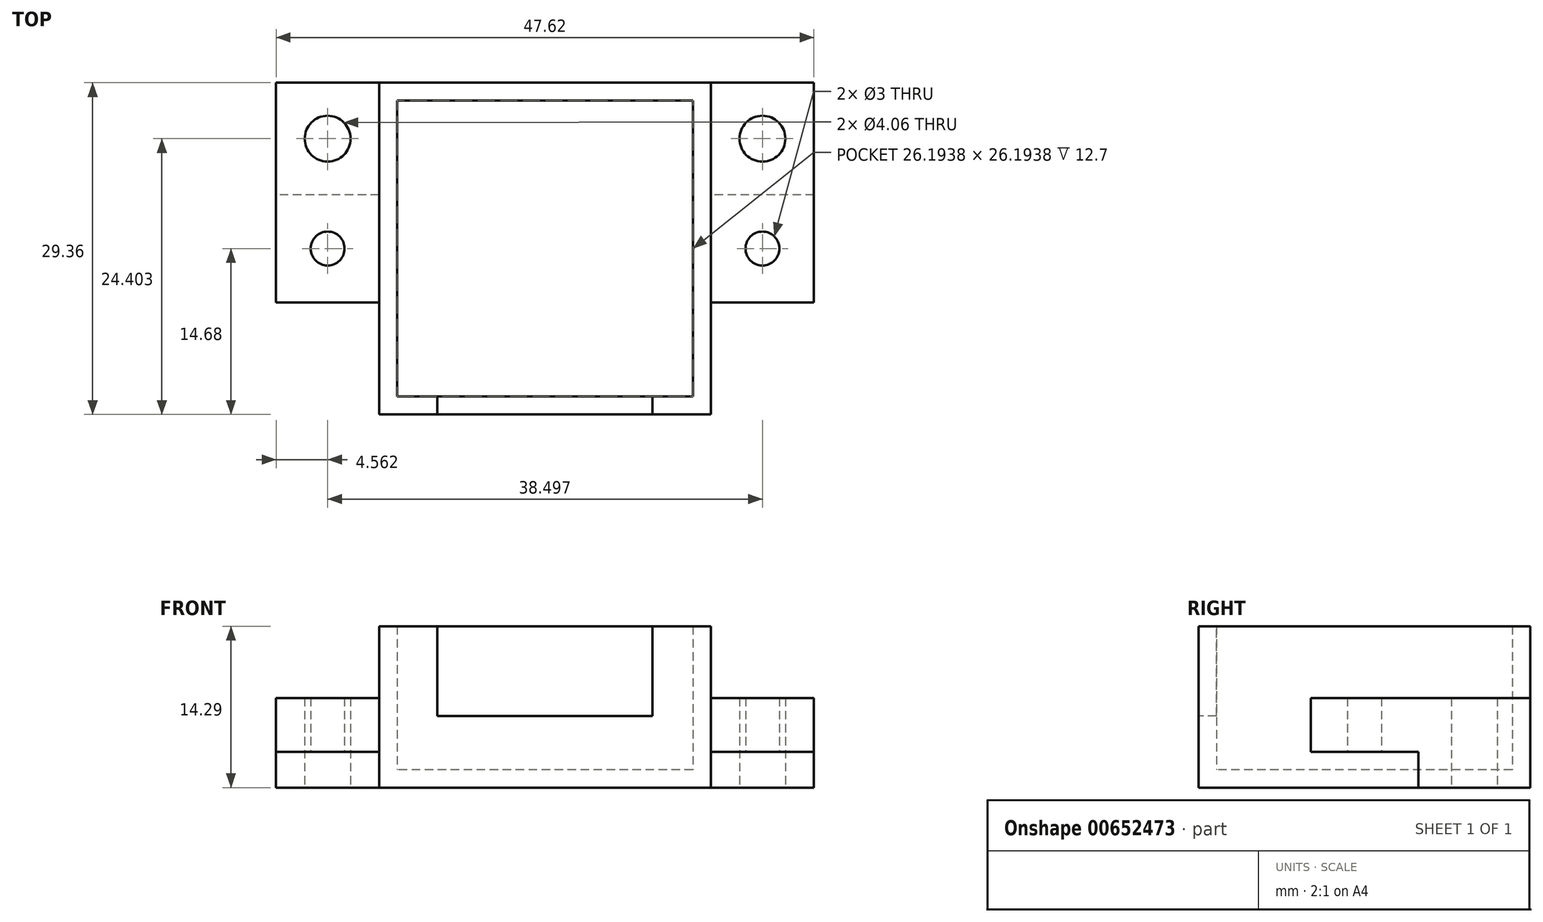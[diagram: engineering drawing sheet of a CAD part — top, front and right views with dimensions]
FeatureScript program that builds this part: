
annotation { "Feature Type Name" : "Feature", "Feature Type Description" : "" }
export const myFeature = defineFeature(function(context is Context, id is Id, definition is map)
    precondition{}
    {
        {
            var Q0;
            Q0=qCreatedBy(makeId("Top.planeOp"),FACE);
            var sketch = newSketch(context, id + "F0", { "sketchPlane" : qUnion([Q0])});
            skLineSegment(sketch, "E0.bottom", {"start": v(13.1, 13.1) * mm, "end": v(-13.1, 13.1) * mm});
            skLineSegment(sketch, "E0.top", {"start": v(13.1, -13.1) * mm, "end": v(-13.1, -13.1) * mm});
            skLineSegment(sketch, "E0.left", {"start": v(13.1, 13.1) * mm, "end": v(13.1, -13.1) * mm});
            skLineSegment(sketch, "E0.right", {"start": v(-13.1, 13.1) * mm, "end": v(-13.1, -13.1) * mm});
            skPoint(sketch, "E0.middle", {"position": v(0, 0) * mm});
            skLineSegment(sketch, "E1.bottom", {"start": v(14.68, 14.68) * mm, "end": v(-14.68, 14.68) * mm});
            skLineSegment(sketch, "E1.top", {"start": v(14.68, -14.68) * mm, "end": v(-14.68, -14.68) * mm});
            skLineSegment(sketch, "E1.left", {"start": v(14.68, 14.68) * mm, "end": v(14.68, -14.68) * mm});
            skLineSegment(sketch, "E1.right", {"start": v(-14.68, 14.68) * mm, "end": v(-14.68, -14.68) * mm});
            skSolve(sketch);
        }
        {
            var Q0;
            Q0=qSketchRegion(id+"F0",true);
            extrude(context, id + "F1", {"entities" : qUnion([Q0]), "depth" : 14.29 * mm, "offsetDistance" : 25.4 * mm});
        }
        {
            var Q0;
            Q0=makeQuery(id+"F1.opExtrude","CAP_FACE",FACE,{"disambiguationData":[OSD([sQuery(id+"F0.wireOp",EDGE,"E0.bottom"),sQuery(id+"F0.wireOp",EDGE,"E0.top"),sQuery(id+"F0.wireOp",EDGE,"E0.left"),sQuery(id+"F0.wireOp",EDGE,"E0.right"),sQuery(id+"F0.wireOp",EDGE,"E1.bottom"),sQuery(id+"F0.wireOp",EDGE,"E1.top"),sQuery(id+"F0.wireOp",EDGE,"E1.left"),sQuery(id+"F0.wireOp",EDGE,"E1.right")])],"isStart":true});
            var sketch = newSketch(context, id + "F2", { "sketchPlane" : qUnion([Q0])});
            skLineSegment(sketch, "E2.bottom", {"start": v(13.1, 13.1) * mm, "end": v(-13.1, 13.1) * mm});
            skLineSegment(sketch, "E2.top", {"start": v(13.1, -13.1) * mm, "end": v(-13.1, -13.1) * mm});
            skLineSegment(sketch, "E2.left", {"start": v(13.1, 13.1) * mm, "end": v(13.1, -13.1) * mm});
            skLineSegment(sketch, "E2.right", {"start": v(-13.1, 13.1) * mm, "end": v(-13.1, -13.1) * mm});
            skPoint(sketch, "E2.middle", {"position": v(0, 0) * mm});
            skSolve(sketch);
        }
        {
            var Q0;
            Q0=makeQuery(id+"F2.imprint","IMPRINT",FACE,{"disambiguationData":[TD([[makeQuery(id+"F2.imprint","IMPRINT",EDGE,{"derivedFrom":sQuery(id+"F2.wireOp",EDGE,"E2.bottom")}),1.0]])]});
            extrude(context, id + "F3", {"entities" : qUnion([Q0]), "oppositeDirection" : true, "depth" : 1.59 * mm, "offsetDistance" : 25.4 * mm});
        }
        {
            var Q0;
            Q0=makeQuery(id+"F1.opExtrude","SWEPT_BODY",BODY,{"disambiguationData":[OSD([sQuery(id+"F0.wireOp",EDGE,"E0.bottom"),sQuery(id+"F0.wireOp",EDGE,"E0.top"),sQuery(id+"F0.wireOp",EDGE,"E0.left"),sQuery(id+"F0.wireOp",EDGE,"E0.right"),sQuery(id+"F0.wireOp",EDGE,"E1.bottom"),sQuery(id+"F0.wireOp",EDGE,"E1.top"),sQuery(id+"F0.wireOp",EDGE,"E1.left"),sQuery(id+"F0.wireOp",EDGE,"E1.right")])]});
            var Q1;
            Q1=makeQuery(id+"F3.opExtrude","SWEPT_BODY",BODY,{"disambiguationData":[OSD([sQuery(id+"F2.wireOp",EDGE,"E2.bottom"),sQuery(id+"F2.wireOp",EDGE,"E2.top"),sQuery(id+"F2.wireOp",EDGE,"E2.left"),sQuery(id+"F2.wireOp",EDGE,"E2.right")])]});
            booleanBodies(context, id + "F4", {"operationType" : BooleanOperationType.UNION, "tools" : qUnion([Q0, Q1])});
        }
        {
            var Q0;
            Q0=qCreatedBy(makeId("Front.planeOp"),FACE);
            var sketch = newSketch(context, id + "F5", { "sketchPlane" : qUnion([Q0])});
            skLineSegment(sketch, "E3", {"start": v(0, 0) * mm, "end": v(0, 14.29) * mm});
            skSolve(sketch);
        }
        {
            var Q0;
            Q0=makeQuery(id+"F10.boolean.opBoolean","MERGE",FACE,{"derivedFrom":[makeQuery(id+"F4.opBoolean","MERGE",FACE,{"derivedFrom":[makeQuery(id+"F1.opExtrude","CAP_FACE",FACE,{"disambiguationData":[OSD([sQuery(id+"F0.wireOp",EDGE,"E0.bottom"),sQuery(id+"F0.wireOp",EDGE,"E0.top"),sQuery(id+"F0.wireOp",EDGE,"E0.left"),sQuery(id+"F0.wireOp",EDGE,"E0.right"),sQuery(id+"F0.wireOp",EDGE,"E1.bottom"),sQuery(id+"F0.wireOp",EDGE,"E1.top"),sQuery(id+"F0.wireOp",EDGE,"E1.left"),sQuery(id+"F0.wireOp",EDGE,"E1.right")])],"isStart":true}),makeQuery(id+"F3.opExtrude","CAP_FACE",FACE,{"disambiguationData":[OSD([sQuery(id+"F2.wireOp",EDGE,"E2.bottom"),sQuery(id+"F2.wireOp",EDGE,"E2.top"),sQuery(id+"F2.wireOp",EDGE,"E2.left"),sQuery(id+"F2.wireOp",EDGE,"E2.right")])],"isStart":true})]}),makeQuery(id+"F10.opExtrude","CAP_FACE",FACE,{"disambiguationData":[OSD([sQuery(id+"F9.wireOp",EDGE,"E5"),sQuery(id+"F9.wireOp",EDGE,"pj68QMxI-dQ5g-Vi9y-1i8w-pIa4mgAurgc5"),sQuery(id+"F9.wireOp",EDGE,"Q7GDvrdU-effV-wMkV-7cSP-b3jGwdTzQUTn"),sQuery(id+"F9.wireOp",EDGE,"UX9pR6vD-BCFl-jX1K-istY-aM91zqfUwH73"),sQuery(id+"F9.wireOp",EDGE,"OVSyVqwR-AaFG-taBa-ozku-bfvhvFuvRjsU")])],"isStart":true}),makeQuery(id+"F10.opExtrude","CAP_FACE",FACE,{"disambiguationData":[OSD([sQuery(id+"F9.wireOp",EDGE,"e5c15c79-e619-4b34-b28a-b5df23dfcadb0.MirrorCS"),sQuery(id+"F9.wireOp",EDGE,"e5c15c79-e619-4b34-b28a-b5df23dfcadb1.MirrorCS"),sQuery(id+"F9.wireOp",EDGE,"e5c15c79-e619-4b34-b28a-b5df23dfcadb2.MirrorCS"),sQuery(id+"F9.wireOp",EDGE,"e5c15c79-e619-4b34-b28a-b5df23dfcadb3.MirrorC"),sQuery(id+"F9.wireOp",EDGE,"e5c15c79-e619-4b34-b28a-b5df23dfcadb4.MirrorCS")])],"isStart":true})]});
            cPlane(context, id + "F6", {"entities" : qUnion([Q0]), "cplaneType" : CPlaneType.OFFSET, "offset" : 3.17 * mm, "oppositeDirection" : true, "width" : 152.4 * mm, "height" : 152.4 * mm});
        }
        {
            var Q0;
            Q0=makeQuery(id+"F1.opExtrude","SWEPT_FACE",FACE,{"disambiguationData":[OSD([sQuery(id+"F0.wireOp",EDGE,"E1.top")])]});
            var sketch = newSketch(context, id + "F7", { "sketchPlane" : qUnion([Q0])});
            skLineSegment(sketch, "E4.bottom", {"start": v(9.52, 14.29) * mm, "end": v(-9.53, 14.29) * mm});
            skLineSegment(sketch, "E4.top", {"start": v(9.52, 6.35) * mm, "end": v(-9.53, 6.35) * mm});
            skLineSegment(sketch, "E4.left", {"start": v(9.52, 14.29) * mm, "end": v(9.52, 6.35) * mm});
            skLineSegment(sketch, "E4.right", {"start": v(-9.53, 14.29) * mm, "end": v(-9.53, 6.35) * mm});
            skPoint(sketch, "E4.middle", {"position": v(0, 10.32) * mm});
            skSolve(sketch);
        }
        {
            var Q0;
            Q0=qSketchRegion(id+"F7",true);
            extrude(context, id + "F8", {"entities" : qUnion([Q0]), "operationType" : NewBodyOperationType.REMOVE, "endBound" : BoundingType.UP_TO_NEXT, "oppositeDirection" : true, "depth" : 25.4 * mm, "offsetDistance" : 25.4 * mm});
        }
        {
            var Q0;
            Q0=qCreatedBy(id+"F6.planeOp",FACE);
            var sketch = newSketch(context, id + "F9", { "sketchPlane" : qUnion([Q0])});
            skCircle(sketch, "E5", {"center": v(19.25, 0) * mm, "radius": 1.5 * mm});
            skLineSegment(sketch, "E6", {"start": v(19.25, 4.76) * mm, "end": v(14.68, 4.76) * mm});
            skLineSegment(sketch, "E7", {"start": v(14.68, 4.76) * mm, "end": v(14.68, -4.76) * mm});
            skLineSegment(sketch, "E8", {"start": v(14.68, -4.76) * mm, "end": v(19.25, -4.76) * mm});
            skLineSegment(sketch, "E9.MirrorCS", {"start": v(-14.68, -4.76) * mm, "end": v(-19.25, -4.76) * mm});
            skCircle(sketch, "E10.MirrorC", {"center": v(-19.25, 0) * mm, "radius": 1.5 * mm});
            skLineSegment(sketch, "E11.MirrorCS", {"start": v(-14.68, 4.76) * mm, "end": v(-14.68, -4.76) * mm});
            skLineSegment(sketch, "E12.MirrorCS", {"start": v(-19.25, 4.76) * mm, "end": v(-14.68, 4.76) * mm});
            skLineSegment(sketch, "E13.bottom", {"start": v(19.25, -4.76) * mm, "end": v(23.81, -4.76) * mm});
            skLineSegment(sketch, "E13.top", {"start": v(19.25, 4.76) * mm, "end": v(23.81, 4.76) * mm});
            skLineSegment(sketch, "E13.left", {"start": v(19.25, -4.76) * mm, "end": v(19.25, 4.76) * mm, "construction": true});
            skLineSegment(sketch, "E13.right", {"start": v(23.81, -4.76) * mm, "end": v(23.81, 4.76) * mm});
            skLineSegment(sketch, "E14.MirrorCS", {"start": v(-19.25, -4.76) * mm, "end": v(-23.81, -4.76) * mm});
            skLineSegment(sketch, "E15.MirrorCS", {"start": v(-23.81, -4.76) * mm, "end": v(-23.81, 4.76) * mm});
            skLineSegment(sketch, "E16.MirrorCS", {"start": v(-19.25, 4.76) * mm, "end": v(-23.81, 4.76) * mm});
            skSolve(sketch);
        }
        {
            var Q0;
            Q0 = qSketchRegion(id + "F9", true);
            extrude(context, id + "F10", {"entities" : qUnion([Q0]), "operationType" : NewBodyOperationType.ADD, "oppositeDirection" : true, "depth" : 4.76 * mm, "offsetDistance" : 25.4 * mm});
        }
        {
            var Q0;
            Q0=makeQuery(id+"F4.opBoolean","MERGE",FACE,{"derivedFrom":[makeQuery(id+"F1.opExtrude","CAP_FACE",FACE,{"disambiguationData":[OSD([sQuery(id+"F0.wireOp",EDGE,"E0.bottom"),sQuery(id+"F0.wireOp",EDGE,"E0.top"),sQuery(id+"F0.wireOp",EDGE,"E0.left"),sQuery(id+"F0.wireOp",EDGE,"E0.right"),sQuery(id+"F0.wireOp",EDGE,"E1.bottom"),sQuery(id+"F0.wireOp",EDGE,"E1.top"),sQuery(id+"F0.wireOp",EDGE,"E1.left"),sQuery(id+"F0.wireOp",EDGE,"E1.right")])],"isStart":true}),makeQuery(id+"F3.opExtrude","CAP_FACE",FACE,{"disambiguationData":[OSD([sQuery(id+"F2.wireOp",EDGE,"E2.bottom"),sQuery(id+"F2.wireOp",EDGE,"E2.top"),sQuery(id+"F2.wireOp",EDGE,"E2.left"),sQuery(id+"F2.wireOp",EDGE,"E2.right")])],"isStart":true})]});
            var sketch = newSketch(context, id + "F11", { "sketchPlane" : qUnion([Q0])});
            skCircle(sketch, "E17", {"center": v(-19.25, -9.72) * mm, "radius": 2.03 * mm});
            skLineSegment(sketch, "E18", {"start": v(-19.25, -14.68) * mm, "end": v(-14.68, -14.68) * mm});
            skLineSegment(sketch, "E19", {"start": v(-14.68, -14.68) * mm, "end": v(-14.68, -4.76) * mm});
            skLineSegment(sketch, "E20", {"start": v(-14.68, -4.76) * mm, "end": v(-19.25, -4.76) * mm});
            skCircle(sketch, "E21", {"center": v(-19.25, 0) * mm, "radius": 1.5 * mm, "construction": true});
            skLineSegment(sketch, "E22", {"start": v(-19.25, -14.68) * mm, "end": v(-19.25, -4.76) * mm, "construction": true});
            skLineSegment(sketch, "E23", {"start": v(-19.25, -14.68) * mm, "end": v(-23.81, -14.68) * mm});
            skLineSegment(sketch, "E24", {"start": v(-23.81, -14.68) * mm, "end": v(-23.81, -4.76) * mm});
            skLineSegment(sketch, "E25", {"start": v(-23.81, -4.76) * mm, "end": v(-19.25, -4.76) * mm});
            skCircle(sketch, "E26.MirrorC", {"center": v(19.25, -9.72) * mm, "radius": 2.03 * mm});
            skLineSegment(sketch, "E27.MirrorCS", {"start": v(19.25, -14.68) * mm, "end": v(14.68, -14.68) * mm});
            skLineSegment(sketch, "E28.MirrorCS", {"start": v(14.68, -4.76) * mm, "end": v(19.25, -4.76) * mm});
            skLineSegment(sketch, "E29.MirrorCS", {"start": v(19.25, -14.68) * mm, "end": v(19.25, -4.76) * mm, "construction": true});
            skLineSegment(sketch, "E30.MirrorCS", {"start": v(19.25, -14.68) * mm, "end": v(23.81, -14.68) * mm});
            skLineSegment(sketch, "E31.MirrorCS", {"start": v(14.68, -14.68) * mm, "end": v(14.68, -4.76) * mm});
            skLineSegment(sketch, "E32.MirrorCS", {"start": v(23.81, -4.76) * mm, "end": v(19.25, -4.76) * mm});
            skLineSegment(sketch, "E33.MirrorCS", {"start": v(23.81, -14.68) * mm, "end": v(23.81, -4.76) * mm});
            skSolve(sketch);
        }
        {
            var Q0;
            Q0 = qSketchRegion(id + "F11", true);
            var Q1;
            Q1=makeQuery(id+"F10.opExtrude","CAP_FACE",FACE,{"disambiguationData":[OSD([sQuery(id+"F9.wireOp",EDGE,"E9.MirrorCS"),sQuery(id+"F9.wireOp",EDGE,"E10.MirrorC"),sQuery(id+"F9.wireOp",EDGE,"E11.MirrorCS"),sQuery(id+"F9.wireOp",EDGE,"E12.MirrorCS"),sQuery(id+"F9.wireOp",EDGE,"E14.MirrorCS"),sQuery(id+"F9.wireOp",EDGE,"E15.MirrorCS"),sQuery(id+"F9.wireOp",EDGE,"E16.MirrorCS")])],"isStart":false});
            extrude(context, id + "F12", {"entities" : qUnion([Q0]), "operationType" : NewBodyOperationType.ADD, "endBound" : BoundingType.UP_TO_SURFACE, "oppositeDirection" : true, "depth" : 25.4 * mm, "endBoundEntityFace" : qUnion([Q1]), "offsetDistance" : 25.4 * mm});
        }
    });
